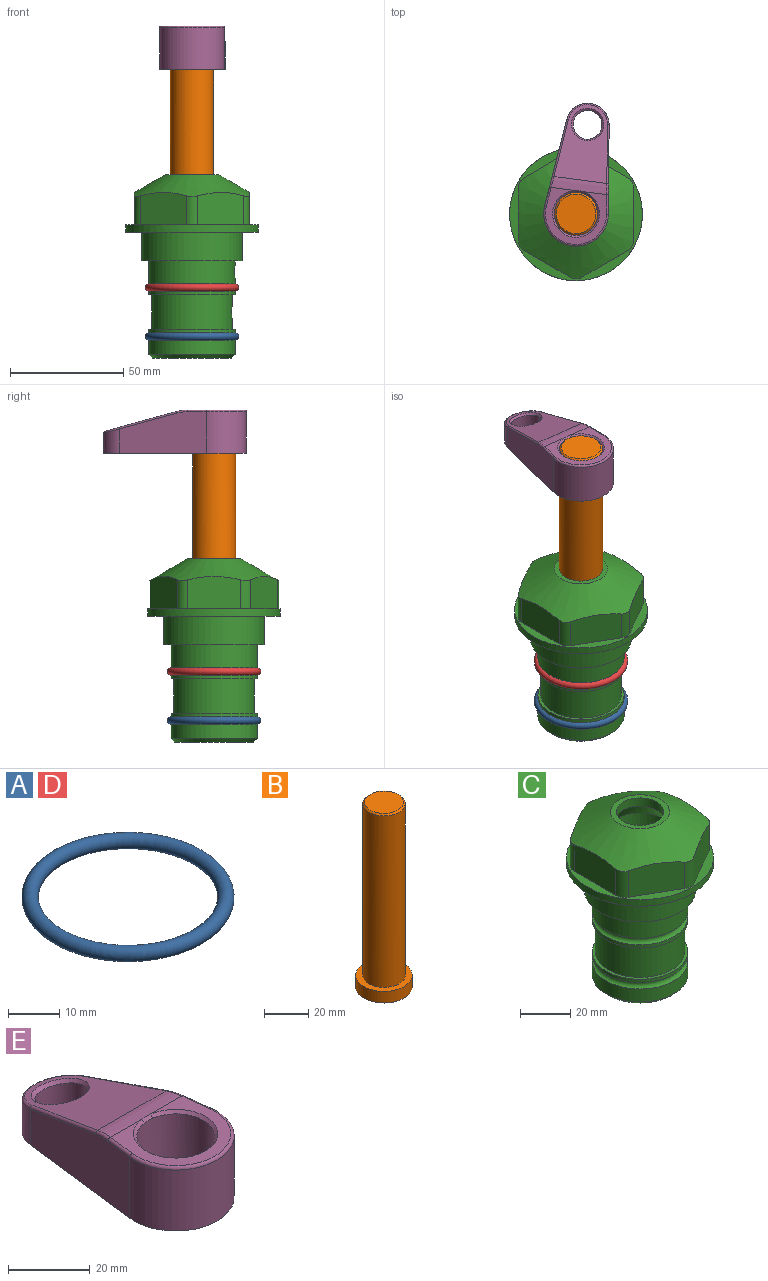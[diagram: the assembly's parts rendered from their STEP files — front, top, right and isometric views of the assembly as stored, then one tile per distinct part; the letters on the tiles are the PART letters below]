
ASSEMBLY  parts=5 mates=4
PART A: 1 faces, bbox 44.7x44.7x3.2 mm
  f0: torus R=19.05mm, axis (0,0,1), area 1193.9mm2
PART B: 6 faces, bbox 25.4x25.4x101.6 mm
  f0: plane 17.46x17.46mm, normal (0,0,1), area 239.5mm2, adj f5
  f1: plane 25.4x25.4mm, normal (0,0,-1), area 506.7mm2, adj f2
  f2: cylinder r=12.7mm len=25.4mm, axis (0,0,1), area 506.7mm2, adj f1,f3
  f3: plane 25.4x25.4mm, normal (0,0,1), area 221.7mm2, adj f2,f4
  f4: cylinder r=9.53mm len=94.46mm, axis (0,0,1), area 5653mm2, adj f3,f5
  f5: cone r=8.73mm half-angle=45deg, axis (0,0,-1), area 64.4mm2, adj f0,f4
PART C: 36 faces, bbox 58.7x58.7x81 mm
  f0: cylinder r=17.78mm len=35.56mm, axis (0,0,1), area 1670.8mm2, adj f23,f24,f31
  f1: cylinder r=19.05mm len=38.1mm, axis (0,0,1), area 1191.9mm2, adj f26,f27,f30
  f2: plane 58.66x58.66mm, normal (0,0,-1), area 1150.6mm2, adj f3,f28
  f3: cylinder r=29.33mm len=58.66mm, axis (0,0,-1), area 585.1mm2, adj f2,f4
  f4: plane 58.66x58.66mm, normal (0,0,1), area 475.9mm2, adj f3,f5,f6,f7,f8,f9,f10,f11
  f5: plane 20.32x14.34mm, normal (-0.5,0.87,0), area 324.4mm2, adj f4,f15,f16,f17
  f6: plane 20.32x14.34mm, normal (0.5,0.87,0), area 324.4mm2, adj f4,f14,f15,f17
  f7: plane 23.48x14.34mm, normal (1,0,0), area 324.4mm2, adj f4,f13,f14,f17
  f8: plane 20.32x14.34mm, normal (0.5,-0.87,0), area 324.4mm2, adj f4,f12,f13,f17
  f9: plane 20.32x14.34mm, normal (-0.5,-0.87,0), area 324.4mm2, adj f4,f11,f12,f17
  f10: plane 23.48x14.34mm, normal (-1,0,0), area 324.4mm2, adj f4,f11,f16,f17
  f11: cylinder r=5.08mm len=12.85mm, axis (0,0,-1), area 67.2mm2, adj f4,f9,f10,f17
  f12: cylinder r=5.08mm len=12.85mm, axis (0,0,-1), area 67.2mm2, adj f4,f8,f9,f17
  f13: cylinder r=5.08mm len=12.85mm, axis (0,0,-1), area 67.2mm2, adj f4,f7,f8,f17
  f14: cylinder r=5.08mm len=12.85mm, axis (0,0,-1), area 67.2mm2, adj f4,f6,f7,f17
  f15: cylinder r=5.08mm len=12.85mm, axis (0,0,-1), area 67.2mm2, adj f4,f5,f6,f17
  f16: cylinder r=5.08mm len=12.85mm, axis (0,0,-1), area 67.2mm2, adj f4,f5,f10,f17
  f17: cone r=11.73mm half-angle=60deg, axis (0,0,-1), area 2071.8mm2, adj f5,f6,f7,f8,f9,f10,f11,f12
  f18: plane 23.46x23.46mm, normal (0,0,1), area 147.4mm2, adj f17,f35
  f19: plane 34.93x34.93mm, normal (0,0,-1), area 958mm2, adj f29
  f20: cylinder r=19.05mm len=38.1mm, axis (0,0,1), area 760.1mm2, adj f21,f29
  f21: torus R=19.05mm, axis (0,0,1), area 565.3mm2, adj f20,f22
  f22: cylinder r=19.05mm len=38.1mm, axis (0,0,1), area 190mm2, adj f21,f23
  f23: plane 38.1x38.1mm, normal (0,0,1), area 146.9mm2, adj f0,f22
  f24: plane 38.1x38.1mm, normal (0,0,-1), area 146.9mm2, adj f0,f25
  f25: cylinder r=19.05mm len=38.1mm, axis (0,0,1), area 190mm2, adj f24,f26
  f26: torus R=19.05mm, axis (0,0,1), area 565.3mm2, adj f1,f25
  f27: plane 44.45x44.45mm, normal (0,0,-1), area 411.7mm2, adj f1,f28
  f28: cylinder r=22.23mm len=44.45mm, axis (0,0,1), area 1773.5mm2, adj f2,f27
  f29: cone r=19.05mm half-angle=45deg, axis (0,0,1), area 257.5mm2, adj f19,f20
  f30: cylinder r=3.17mm len=6.75mm, axis (-1,0,0), area 128mm2, adj f1,f33
  f31: cylinder r=3.17mm len=6.35mm, axis (-1,0,0), area 102.5mm2, adj f0,f33
  f32: plane 25.4x25.4mm, normal (0,0,1), area 506.7mm2, adj f33
  f33: cylinder r=12.7mm len=66.42mm, axis (0,0,-1), area 5236.2mm2, adj f30,f31,f32,f34
  f34: cone r=9.53mm half-angle=30deg, axis (0,0,-1), area 443.4mm2, adj f33,f35
  f35: cylinder r=9.53mm len=19.05mm, axis (0,0,-1), area 240.9mm2, adj f18,f34
PART D: same geometry as A
PART E: 31 faces, bbox 31.7x65.5x19.8 mm
  f0: plane 39.12x18.26mm, normal (0.99,0.12,0), area 612.2mm2, adj f1,f4,f7,f11,f13,f15
  f1: cylinder r=9.53mm len=18.91mm, axis (0,0,-1), area 296.1mm2, adj f0,f2,f7,f17
  f2: plane 39.12x18.26mm, normal (-0.99,0.12,0), area 612.2mm2, adj f1,f4,f7,f12,f14,f16
  f3: cylinder r=6.35mm len=12.7mm, axis (0,0,-1), area 362.4mm2, adj f7,f18
  f4: cylinder r=14.29mm len=28.58mm, axis (0,0,-1), area 882.2mm2, adj f0,f2,f7,f10
  f5: cylinder r=9.53mm len=19.05mm, axis (0,0,-1), area 1092.6mm2, adj f7,f19,f20
  f6: plane 26.99x23.69mm, normal (0,0,1), area 216.2mm2, adj f9,f10,f11,f12,f19
  f7: plane 63.5x28.58mm, normal (0,0,-1), area 661.8mm2, adj f0,f1,f2,f3,f4,f5,f22,f23
  f8: plane 33.52x23.6mm, normal (0,0.26,0.97), area 486mm2, adj f9,f15,f16,f17,f18
  f9: cylinder r=19.05mm len=24.72mm, axis (1,0,0), area 120.4mm2, adj f6,f8,f13,f14,f20
  f10: torus R=13.49mm, axis (0,0,1), area 59mm2, adj f4,f6,f11,f12
  f11: cylinder r=0.79mm len=8.67mm, axis (0.12,-0.99,0), area 10.8mm2, adj f0,f6,f10,f13
  f12: cylinder r=0.79mm len=8.67mm, axis (0.12,0.99,0), area 10.8mm2, adj f2,f6,f10,f14
  f13: bspline ~4.95x1.42mm, area 6.1mm2, adj f0,f9,f11,f15
  f14: bspline ~4.95x1.42mm, area 6.1mm2, adj f2,f9,f12,f16
  f15: cylinder r=0.79mm len=25.95mm, axis (0.12,-0.96,0.26), area 32.9mm2, adj f0,f8,f13,f17
  f16: cylinder r=0.79mm len=25.95mm, axis (0.12,0.96,-0.26), area 32.9mm2, adj f2,f8,f14,f17
  f17: bspline ~18.91x8.38mm, area 30mm2, adj f1,f8,f15,f16
  f18: bspline ~14.29x14.29mm, area 48.3mm2, adj f3,f8
  f19: cone r=9.53mm half-angle=45deg, axis (0,0,1), area 66.5mm2, adj f5,f6,f20
  f20: bspline ~3.22x0.96mm, area 3.5mm2, adj f5,f9,f19
  f21: plane 2.75x2.72mm, normal (0,0,-1), area 2.9mm2, adj f23,f25,f28
  f22: plane 23.05x15.88mm, normal (-0.99,-0.12,0), area 323.6mm2, adj f7,f25,f26,f27,f28,f29
  f23: plane 23.05x15.88mm, normal (0.99,-0.12,0), area 323.6mm2, adj f7,f21,f25,f27,f28,f30
  f24: cylinder r=9.53mm len=10.69mm, axis (0,0,-1), area 114.7mm2, adj f7,f27,f29,f30
  f25: cylinder r=12.7mm len=20.59mm, axis (0,0,-1), area 381.1mm2, adj f7,f21,f22,f23,f26,f28
  f26: plane 2.75x2.72mm, normal (0,0,-1), area 2.9mm2, adj f22,f25,f28
  f27: plane 19.72x18.37mm, normal (0,-0.26,-0.97), area 291.8mm2, adj f22,f23,f24,f28,f29,f30
  f28: cylinder r=15.88mm len=19.92mm, axis (1,0,0), area 54.8mm2, adj f21,f22,f23,f25,f26,f27
  f29: cylinder r=1.59mm len=11mm, axis (0,0,-1), area 34.7mm2, adj f7,f22,f24,f27
  f30: cylinder r=1.59mm len=11mm, axis (0,0,-1), area 34.7mm2, adj f7,f23,f24,f27
PLACE A t=(0,0,-21.59)mm
PLACE B rot(axis=(0,0,-1),7.4deg) t=(0,0,27.55)mm
PLACE C at identity fixed
PLACE D at identity
PLACE E rot(axis=(0,0,-1),7.4deg) t=(0,0,27.55)mm
MATE fastened B.f2 <-> E.f4  axis (0,0,1) through (0,0,91.05)mm
MATE fastened D.f0 <-> C.f0  axis (0,0,1) through (0,0,-24.51)mm
MATE cylindrical B.f2 <-> C.f0  axis (0,0,-1) through (0,0,-10.55)mm
MATE fastened A.f0 <-> C.f0  axis (0,0,1) through (0,0,-46.1)mm
